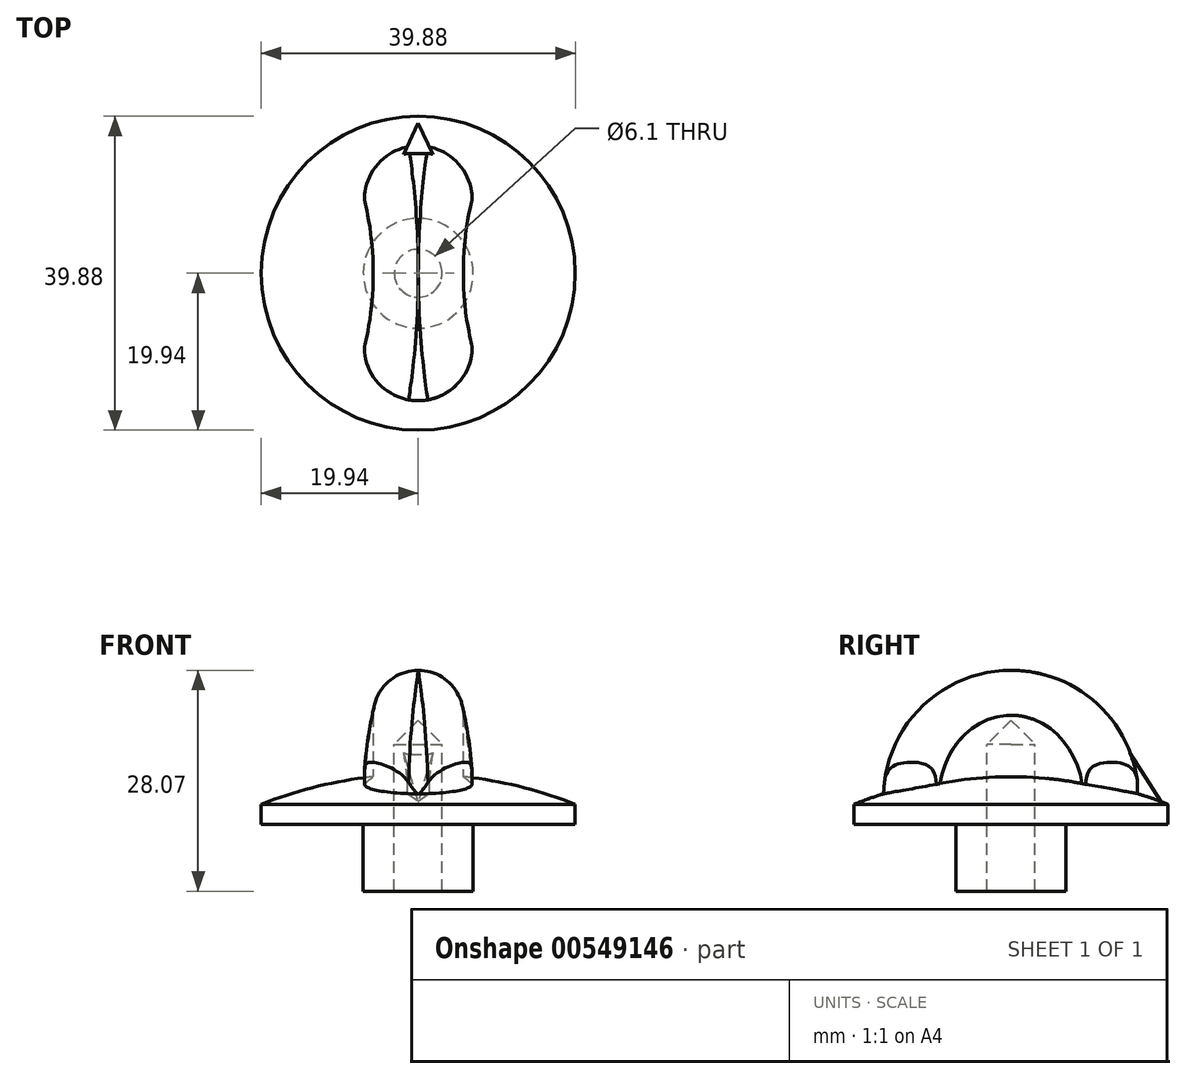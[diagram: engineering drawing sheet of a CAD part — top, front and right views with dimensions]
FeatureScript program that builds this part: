
annotation { "Feature Type Name" : "Feature", "Feature Type Description" : "" }
export const myFeature = defineFeature(function(context is Context, id is Id, definition is map)
    precondition{}
    {
        {
            var Q0;
            Q0=qCreatedBy(makeId("Top.planeOp"),FACE);
            var sketch = newSketch(context, id + "F0", { "sketchPlane" : qUnion([Q0])});
            skCircle(sketch, "E0", {"center": v(0, 0) * mm, "radius": 6.99 * mm});
            skCircle(sketch, "E1", {"center": v(0, 0) * mm, "radius": 3.05 * mm});
            skSolve(sketch);
        }
        {
            var Q0;
            Q0 = qSketchRegion(id + "F0", true);
            extrude(context, id + "F1", {"entities" : qUnion([Q0]), "oppositeDirection" : true, "depth" : 8.5 * mm, "offsetDistance" : 25.4 * mm});
        }
        {
            var Q0;
            Q0=makeQuery(id+"F1.opExtrude","CAP_FACE",FACE,{"disambiguationData":[OSD([sQuery(id+"F0.wireOp",EDGE,"E0"),sQuery(id+"F0.wireOp",EDGE,"E1")])],"isStart":false});
            var sketch = newSketch(context, id + "F2", { "sketchPlane" : qUnion([Q0])});
            skLineSegment(sketch, "E2", {"start": v(-2.98, 0.64) * mm, "end": v(2.98, 0.64) * mm});
            skLineSegment(sketch, "E3.bottom", {"start": v(-6.99, 0.64) * mm, "end": v(6.99, 0.64) * mm});
            skLineSegment(sketch, "E3.top", {"start": v(-6.99, -0.64) * mm, "end": v(6.99, -0.64) * mm});
            skLineSegment(sketch, "E3.left", {"start": v(-6.99, 0.64) * mm, "end": v(-6.99, -0.64) * mm});
            skLineSegment(sketch, "E3.right", {"start": v(6.99, 0.64) * mm, "end": v(6.99, -0.64) * mm});
            skLineSegment(sketch, "E4", {"start": v(0, 0.64) * mm, "end": v(0, -0.64) * mm, "construction": true});
            skSolve(sketch);
        }
        {
            var Q0;
            {var subQ0=sQuery(id+"F2.wireOp",EDGE,"E3.left");var subQ1=sQuery(id+"F2.wireOp",EDGE,"E3.bottom");var subQ2=makeQuery(id+"F2.imprint","INTERSECT",VERTEX,{"derivedFrom":[subQ1,subQ0]});Q0=makeQuery(id+"F2.imprint","IMPRINT",FACE,{"disambiguationData":[TD([[makeQuery(id+"F2.imprint","IMPRINT",EDGE,{"disambiguationData":[TD([[subQ2,-1.0]])],"derivedFrom":subQ1}),-1.0]])]});}
            var Q1;
            {var subQ0=sQuery(id+"F2.wireOp",EDGE,"E3.right");var subQ1=sQuery(id+"F2.wireOp",EDGE,"E3.bottom");var subQ2=makeQuery(id+"F2.imprint","INTERSECT",VERTEX,{"derivedFrom":[subQ1,subQ0]});Q1=makeQuery(id+"F2.imprint","IMPRINT",FACE,{"disambiguationData":[TD([[makeQuery(id+"F2.imprint","IMPRINT",EDGE,{"disambiguationData":[TD([[subQ2,1.0]])],"derivedFrom":subQ1}),-1.0]])]});}
            var Q2;
            {var subQ0=sQuery(id+"F2.wireOp",EDGE,"E3.left");var subQ1=sQuery(id+"F2.wireOp",EDGE,"E3.top");var subQ2=makeQuery(id+"F2.imprint","INTERSECT",VERTEX,{"derivedFrom":[subQ1,subQ0]});Q2=makeQuery(id+"F2.imprint","IMPRINT",FACE,{"disambiguationData":[TD([[makeQuery(id+"F2.imprint","IMPRINT",EDGE,{"disambiguationData":[TD([[subQ2,-1.0]])],"derivedFrom":subQ1}),1.0]])]});}
            var Q3;
            {var subQ0=sQuery(id+"F2.wireOp",EDGE,"E3.right");var subQ1=sQuery(id+"F2.wireOp",EDGE,"E3.top");var subQ2=makeQuery(id+"F2.imprint","INTERSECT",VERTEX,{"derivedFrom":[subQ1,subQ0]});Q3=makeQuery(id+"F2.imprint","IMPRINT",FACE,{"disambiguationData":[TD([[makeQuery(id+"F2.imprint","IMPRINT",EDGE,{"disambiguationData":[TD([[subQ2,1.0]])],"derivedFrom":subQ1}),1.0]])]});}
            var Q4;
            {var subQ0=sQuery(id+"F2.wireOp",EDGE,"E3.bottom");var subQ1=makeQuery(id+"F1.opExtrude","CAP_EDGE",EDGE,{"disambiguationData":[OSD([sQuery(id+"F0.wireOp",EDGE,"E1")])],"isStart":false});var subQ2=makeQuery(id+"F2.imprint","INTERSECT",VERTEX,{"disambiguationData":[OD(0.0)],"derivedFrom":[subQ1,subQ0]});Q4=makeQuery(id+"F2.imprint","IMPRINT",FACE,{"disambiguationData":[TD([[makeQuery(id+"F2.imprint","IMPRINT",EDGE,{"disambiguationData":[TD([[subQ2,-1.0]])],"derivedFrom":subQ0}),-1.0]])]});}
            var Q5;
            {var subQ1=makeQuery(id+"F1.opExtrude","CAP_EDGE",EDGE,{"disambiguationData":[OSD([sQuery(id+"F0.wireOp",EDGE,"E0")])],"isStart":false});var subQ6=sQuery(id+"F2.wireOp",EDGE,"E3.bottom");var subQ7=makeQuery(id+"F2.imprint","INTERSECT",VERTEX,{"disambiguationData":[OD(1.0)],"derivedFrom":[subQ1,subQ6]});Q5=makeQuery(id+"F2.imprint","IMPRINT",FACE,{"disambiguationData":[TD([[makeQuery(id+"F2.imprint","IMPRINT",EDGE,{"disambiguationData":[TD([[subQ7,1.0]])],"derivedFrom":subQ6}),-1.0]])]});}
            var Q6;
            {var subQ1=makeQuery(id+"F1.opExtrude","CAP_EDGE",EDGE,{"disambiguationData":[OSD([sQuery(id+"F0.wireOp",EDGE,"E0")])],"isStart":false});var subQ4=sQuery(id+"F2.wireOp",EDGE,"E3.bottom");var subQ5=makeQuery(id+"F2.imprint","INTERSECT",VERTEX,{"disambiguationData":[OD(0.0)],"derivedFrom":[subQ1,subQ4]});Q6=makeQuery(id+"F2.imprint","IMPRINT",FACE,{"disambiguationData":[TD([[makeQuery(id+"F2.imprint","IMPRINT",EDGE,{"disambiguationData":[TD([[subQ5,-1.0]])],"derivedFrom":subQ4}),-1.0]])]});}
            extrude(context, id + "F3", {"entities" : qUnion([Q0, Q1, Q2, Q3, Q4, Q5, Q6]), "operationType" : NewBodyOperationType.REMOVE, "oppositeDirection" : true, "depth" : 4.32 * mm, "offsetDistance" : 25.4 * mm});
        }
        {
            var Q0;
            Q0=qCreatedBy(makeId("Right.planeOp"),FACE);
            var sketch = newSketch(context, id + "F4", { "sketchPlane" : qUnion([Q0])});
            skLineSegment(sketch, "E5", {"start": v(0, 0) * mm, "end": v(-19.94, 0) * mm});
            skLineSegment(sketch, "E6", {"start": v(-19.94, 0) * mm, "end": v(-19.94, 2.54) * mm});
            skArc(sketch, "E7", {"start": v(0, 6.35) * mm, "mid": v(-10.15, 5.39) * mm, "end": v(-19.94, 2.54) * mm});
            skLineSegment(sketch, "E8", {"start": v(0, 6.35) * mm, "end": v(0, 0) * mm});
            skLineSegment(sketch, "E9", {"start": v(0, 6.35) * mm, "end": v(2.72, 6.35) * mm, "construction": true});
            skSolve(sketch);
        }
        {
            var Q0;
            Q0=makeQuery(id+"F4.imprint","IMPRINT",FACE,{"disambiguationData":[TD([[makeQuery(id+"F4.imprint","IMPRINT",EDGE,{"derivedFrom":sQuery(id+"F4.wireOp",EDGE,"E5")}),-1.0]])]});
            var Q1;
            Q1=sQuery(id+"F4.wireOp",EDGE,"E8");
            revolve(context, id + "F5", {"operationType" : NewBodyOperationType.ADD, "entities" : qUnion([Q0]), "axis" : qUnion([Q1]), "revolveType" : RevolveType.FULL});
        }
        {
            var Q0;
            Q0=qCreatedBy(makeId("Top.planeOp"),FACE);
            cPlane(context, id + "F6", {"entities" : qUnion([Q0]), "cplaneType" : CPlaneType.OFFSET, "offset" : 2.54 * mm, "width" : 152.4 * mm, "height" : 152.4 * mm});
        }
        {
            var Q0;
            Q0=qCreatedBy(id+"F6.planeOp",FACE);
            var sketch = newSketch(context, id + "F7", { "sketchPlane" : qUnion([Q0])});
            skCircle(sketch, "E10", {"center": v(0, 0) * mm, "radius": 16.2 * mm, "construction": true});
            skLineSegment(sketch, "E11.bottom", {"start": v(6.86, 16.2) * mm, "end": v(-6.86, 16.2) * mm, "construction": true});
            skLineSegment(sketch, "E11.top", {"start": v(6.86, -16.2) * mm, "end": v(-6.86, -16.2) * mm, "construction": true});
            skLineSegment(sketch, "E11.left", {"start": v(6.86, 16.2) * mm, "end": v(6.86, -16.2) * mm, "construction": true});
            skLineSegment(sketch, "E11.right", {"start": v(-6.86, 16.2) * mm, "end": v(-6.86, -16.2) * mm, "construction": true});
            skLineSegment(sketch, "E12.bottom", {"start": v(19.94, 9.4) * mm, "end": v(-19.94, 9.4) * mm, "construction": true});
            skLineSegment(sketch, "E12.top", {"start": v(19.94, -9.4) * mm, "end": v(-19.94, -9.4) * mm, "construction": true});
            skLineSegment(sketch, "E12.left", {"start": v(19.94, 9.4) * mm, "end": v(19.94, -9.4) * mm, "construction": true});
            skLineSegment(sketch, "E12.right", {"start": v(-19.94, 9.4) * mm, "end": v(-19.94, -9.4) * mm, "construction": true});
            skArc(sketch, "E13", {"start": v(6.86, 9.4) * mm, "mid": v(0, 16.2) * mm, "end": v(-6.86, 9.4) * mm});
            skArc(sketch, "E14", {"start": v(-6.86, -9.4) * mm, "mid": v(0, -16.2) * mm, "end": v(6.86, -9.4) * mm});
            skLineSegment(sketch, "E15.bottom", {"start": v(5.72, 19.94) * mm, "end": v(-5.72, 19.94) * mm, "construction": true});
            skLineSegment(sketch, "E15.top", {"start": v(5.72, -19.94) * mm, "end": v(-5.72, -19.94) * mm, "construction": true});
            skLineSegment(sketch, "E15.left", {"start": v(5.72, 19.94) * mm, "end": v(5.72, -19.94) * mm, "construction": true});
            skLineSegment(sketch, "E15.right", {"start": v(-5.72, 19.94) * mm, "end": v(-5.72, -19.94) * mm, "construction": true});
            skArc(sketch, "E16", {"start": v(-6.86, -9.4) * mm, "mid": v(-5.72, 0) * mm, "end": v(-6.86, 9.4) * mm});
            skArc(sketch, "E17", {"start": v(6.86, 9.4) * mm, "mid": v(5.72, 0) * mm, "end": v(6.86, -9.4) * mm});
            skSolve(sketch);
        }
        {
            var Q0;
            Q0 = qSketchRegion(id + "F7", true);
            extrude(context, id + "F8", {"entities" : qUnion([Q0]), "operationType" : NewBodyOperationType.ADD, "depth" : 17.02 * mm, "offsetDistance" : 25.4 * mm});
        }
        {
            var Q0;
            Q0=qCreatedBy(makeId("Right.planeOp"),FACE);
            var sketch = newSketch(context, id + "F9", { "sketchPlane" : qUnion([Q0])});
            skArc(sketch, "E18", {"start": v(16.2, 3.87) * mm, "mid": v(0, 19.56) * mm, "end": v(-16.2, 3.87) * mm});
            skLineSegment(sketch, "E19", {"start": v(16.2, 3.87) * mm, "end": v(23.27, 20.01) * mm});
            skLineSegment(sketch, "E20", {"start": v(23.27, 20.01) * mm, "end": v(-21.74, 24.5) * mm});
            skLineSegment(sketch, "E21", {"start": v(-21.74, 24.5) * mm, "end": v(-16.2, 3.87) * mm});
            skSolve(sketch);
        }
        {
            var Q0;
            Q0=makeQuery(id+"F9.imprint","IMPRINT",FACE,{"disambiguationData":[TD([[makeQuery(id+"F9.imprint","IMPRINT",EDGE,{"derivedFrom":sQuery(id+"F9.wireOp",EDGE,"E18")}),-1.0]])]});
            extrude(context, id + "F10", {"entities" : qUnion([Q0]), "operationType" : NewBodyOperationType.REMOVE, "endBound" : BoundingType.SYMMETRIC, "oppositeDirection" : true, "depth" : 25.4 * mm, "offsetDistance" : 25.4 * mm});
        }
        {
            var Q0;
            Q0=qCreatedBy(id+"F6.planeOp",FACE);
            var sketch = newSketch(context, id + "F11", { "sketchPlane" : qUnion([Q0])});
            skLineSegment(sketch, "E22", {"start": v(-2.96, 12.7) * mm, "end": v(0, 19.05) * mm});
            skLineSegment(sketch, "E23", {"start": v(0, 19.05) * mm, "end": v(2.96, 12.7) * mm});
            skLineSegment(sketch, "E24", {"start": v(0, 19.05) * mm, "end": v(0, 0) * mm, "construction": true});
            skLineSegment(sketch, "E25", {"start": v(-2.96, 12.7) * mm, "end": v(2.96, 12.7) * mm});
            skSolve(sketch);
        }
        {
            var Q0;
            Q0 = qSketchRegion(id + "F11", true);
            extrude(context, id + "F12", {"entities" : qUnion([Q0]), "operationType" : NewBodyOperationType.ADD, "depth" : 6.35 * mm, "offsetDistance" : 25.4 * mm});
        }
        {
            var Q0;
            Q0=qCreatedBy(makeId("Right.planeOp"),FACE);
            var sketch = newSketch(context, id + "F13", { "sketchPlane" : qUnion([Q0])});
            skLineSegment(sketch, "E26", {"start": v(15.23, 8.9) * mm, "end": v(19.05, 2.88) * mm});
            skLineSegment(sketch, "E27", {"start": v(15.23, 8.9) * mm, "end": v(19.05, 8.9) * mm});
            skLineSegment(sketch, "E28", {"start": v(19.05, 8.9) * mm, "end": v(19.05, 2.88) * mm});
            skSolve(sketch);
        }
        {
            var Q0;
            Q0 = qSketchRegion(id + "F13", true);
            extrude(context, id + "F14", {"entities" : qUnion([Q0]), "operationType" : NewBodyOperationType.REMOVE, "endBound" : BoundingType.SYMMETRIC, "oppositeDirection" : true, "depth" : 25.4 * mm, "offsetDistance" : 25.4 * mm});
        }
        {
            var Q0;
            {var subQ0=sQuery(id+"F0.wireOp",EDGE,"E0");var subQ1=sQuery(id+"F0.wireOp",EDGE,"E1");Q0=makeQuery(id+"F3.boolean.opBoolean","SPLIT",FACE,{"disambiguationData":[TD([makeQuery(id+"F3.opExtrude","SWEPT_FACE",FACE,{"disambiguationData":[OSD([sQuery(id+"F2.wireOp",EDGE,"E3.top")])]})])],"derivedFrom":makeQuery(id+"F1.opExtrude","CAP_FACE",FACE,{"disambiguationData":[OSD([subQ0,subQ1])],"isStart":false})});}
            var sketch = newSketch(context, id + "F15", { "sketchPlane" : qUnion([Q0])});
            skArc(sketch, "E29.0", {"start": v(-2.98, 0.63) * mm, "mid": v(0, 3.05) * mm, "end": v(2.98, 0.64) * mm});
            skArc(sketch, "E29.1", {"start": v(2.98, -0.64) * mm, "mid": v(0, -3.05) * mm, "end": v(-2.98, -0.64) * mm});
            skArc(sketch, "E29.2", {"start": v(-2.98, -0.64) * mm, "mid": v(-3.05, 0) * mm, "end": v(-2.98, 0.64) * mm});
            skArc(sketch, "E29.3", {"start": v(2.98, 0.63) * mm, "mid": v(3.05, 0) * mm, "end": v(2.98, -0.64) * mm});
            skSolve(sketch);
        }
        {
            var Q0;
            Q0 = qSketchRegion(id + "F15", true);
            extrude(context, id + "F16", {"entities" : qUnion([Q0]), "operationType" : NewBodyOperationType.REMOVE, "oppositeDirection" : true, "depth" : 21.72 * mm, "offsetDistance" : 25.4 * mm});
        }
        {
            var Q0;
            Q0=makeQuery(id+"F10.boolean.opBoolean","INTERSECT",EDGE,{"derivedFrom":[makeQuery(id+"F8.opExtrude","SWEPT_FACE",FACE,{"disambiguationData":[OSD([sQuery(id+"F7.wireOp",EDGE,"E17")])]}),makeQuery(id+"F10.opExtrude","SWEPT_FACE",FACE,{"disambiguationData":[OSD([sQuery(id+"F9.wireOp",EDGE,"E18")])]})]});
            var Q1;
            Q1=makeQuery(id+"F10.boolean.opBoolean","INTERSECT",EDGE,{"derivedFrom":[makeQuery(id+"F8.opExtrude","SWEPT_FACE",FACE,{"disambiguationData":[OSD([sQuery(id+"F7.wireOp",EDGE,"E16")])]}),makeQuery(id+"F10.opExtrude","SWEPT_FACE",FACE,{"disambiguationData":[OSD([sQuery(id+"F9.wireOp",EDGE,"E18")])]})]});
            fillet(context, id + "F17", {"entities" : qUnion([Q0, Q1]), "radius" : 5.7 * mm, "tangentPropagation" : true, "allowEdgeOverflow" : false});
        }
        {
            var Q0;
            Q0=makeQuery(id+"F16.boolean.opBoolean","COPY",EDGE,{"derivedFrom":makeQuery(id+"F16.opExtrude","CAP_EDGE",EDGE,{"disambiguationData":[OSD([sQuery(id+"F15.wireOp",EDGE,"E29.0"),sQuery(id+"F15.wireOp",EDGE,"E29.1"),sQuery(id+"F15.wireOp",EDGE,"E29.2"),sQuery(id+"F15.wireOp",EDGE,"E29.3")])],"isStart":false})});
            chamfer(context, id + "F18", {"entities" : qUnion([Q0]), "width" : 3.05 * mm, "tangentPropagation" : true});
        }
    });
